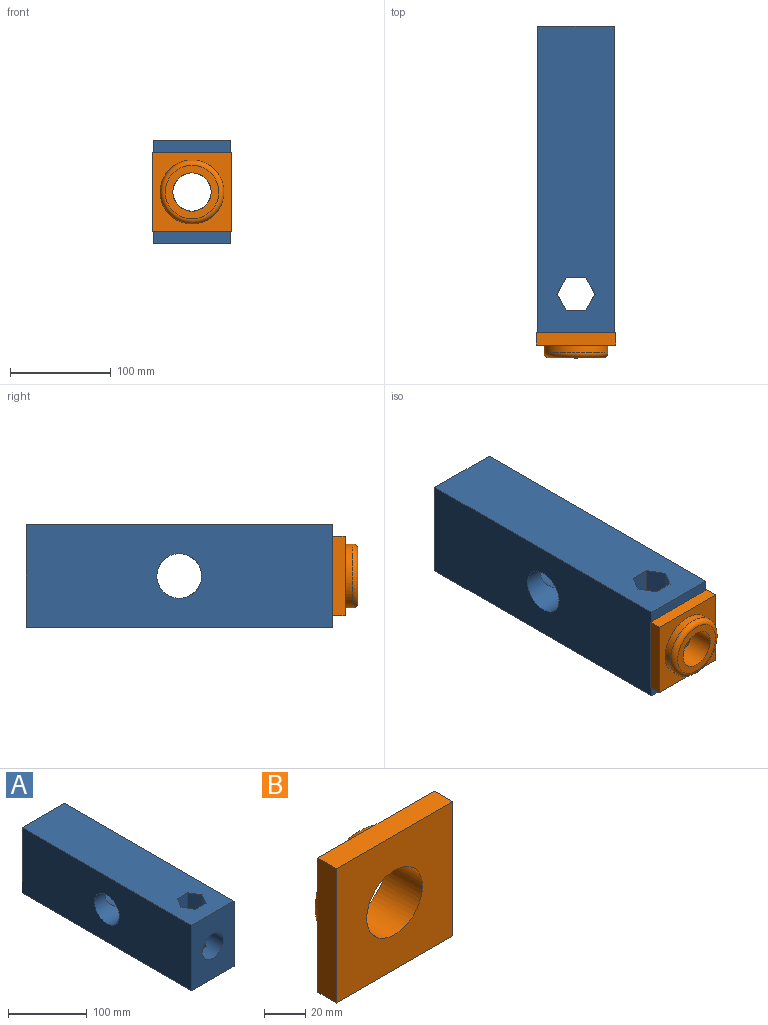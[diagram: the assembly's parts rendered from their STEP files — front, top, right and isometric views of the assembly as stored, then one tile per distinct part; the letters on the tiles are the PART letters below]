
ASSEMBLY  parts=2 mates=1
PART A: 22 faces, bbox 76.2x304.8x101.6 mm
  f0: cylinder r=19.05mm len=38.1mm, axis (0,1,0), area 3446.6mm2, adj f7,f11,f12,f13,f18,f19,f20
  f1: cylinder r=19.05mm len=102.85mm, axis (0,1,0), area 10501.1mm2, adj f9,f10,f14,f15,f16,f17,f21
  f2: plane 304.8x76.2mm, normal (0,0,1), area 22282.9mm2, adj f5,f6,f7,f8,f16,f17,f18,f19
  f3: plane 304.8x76.2mm, normal (0,0,-1), area 22282.9mm2, adj f5,f6,f7,f8,f10,f11,f12,f13
  f4: cylinder r=19.05mm len=140.95mm, axis (0,1,0), area 16173.5mm2, adj f8,f9
  f5: plane 304.8x101.6mm, normal (1,0,0), area 29415.9mm2, adj f2,f3,f7,f8,f9
  f6: plane 304.8x101.6mm, normal (-1,0,0), area 29415.9mm2, adj f2,f3,f7,f8,f9
  f7: plane 101.6x76.2mm, normal (0,-1,0), area 6601.8mm2, adj f0,f2,f3,f5,f6
  f8: plane 101.6x76.2mm, normal (0,1,0), area 6601.8mm2, adj f2,f3,f4,f5,f6
  f9: cylinder r=22.23mm len=76.2mm, axis (-1,0,0), area 8053.1mm2, adj f1,f4,f5,f6
  f10: plane 50.8x16.5mm, normal (-0.87,-0.5,0), area 744.9mm2, adj f1,f3,f11,f15
  f11: plane 50.8x16.5mm, normal (-0.87,0.5,0), area 744.9mm2, adj f0,f3,f10,f12
  f12: plane 34.3x19.05mm, normal (0,1,0), area 620.6mm2, adj f0,f3,f11,f13
  f13: plane 50.8x16.5mm, normal (0.87,0.5,0), area 744.9mm2, adj f0,f3,f12,f14
  f14: plane 50.8x16.5mm, normal (0.87,-0.5,0), area 744.9mm2, adj f1,f3,f13,f15
  f15: plane 34.3x19.05mm, normal (0,-1,0), area 620.6mm2, adj f1,f3,f10,f14
  f16: plane 34.3x19.05mm, normal (0,-1,0), area 620.6mm2, adj f1,f2,f17,f21
  f17: plane 50.8x16.5mm, normal (0.87,-0.5,0), area 744.9mm2, adj f1,f2,f16,f18
  f18: plane 50.8x16.5mm, normal (0.87,0.5,0), area 744.9mm2, adj f0,f2,f17,f19
  f19: plane 34.3x19.05mm, normal (0,1,0), area 620.6mm2, adj f0,f2,f18,f20
  f20: plane 50.8x16.5mm, normal (-0.87,0.5,0), area 744.9mm2, adj f0,f2,f19,f21
  f21: plane 50.8x16.5mm, normal (-0.87,-0.5,0), area 744.9mm2, adj f1,f2,f16,f20
PART B: 10 faces, bbox 79.4x25.4x79.4 mm
  f0: cylinder r=31.75mm len=63.5mm, axis (0,1,0), area 1520.1mm2, adj f2,f7
  f1: plane 53.34x53.34mm, normal (0,1,0), area 1094.5mm2, adj f2,f9
  f2: torus R=26.67mm, axis (0,-1,0), area 1499.3mm2, adj f0,f1
  f3: plane 79.38x12.7mm, normal (0,0,1), area 1008.1mm2, adj f4,f6,f7,f8
  f4: plane 79.38x12.7mm, normal (1,0,0), area 1008.1mm2, adj f3,f5,f7,f8
  f5: plane 79.38x12.7mm, normal (0,0,-1), area 1008.1mm2, adj f4,f6,f7,f8
  f6: plane 79.38x12.7mm, normal (-1,0,0), area 1008.1mm2, adj f3,f5,f7,f8
  f7: plane 79.38x79.38mm, normal (0,1,0), area 3133.5mm2, adj f0,f3,f4,f5,f6
  f8: plane 79.38x79.38mm, normal (0,-1,0), area 5160.3mm2, adj f3,f4,f5,f6,f9
  f9: cylinder r=19.05mm len=38.1mm, axis (0,1,0), area 3040.2mm2, adj f1,f8
PLACE A t=(0.38,-10.91,-22.47)mm
PLACE B rot(axis=(1,0,0),180deg) t=(0.38,-188.71,-22.47)mm
MATE revolute B.f9 <-> A.f0  axis (0,1,0) through (0.38,-163.31,-22.47)mm
